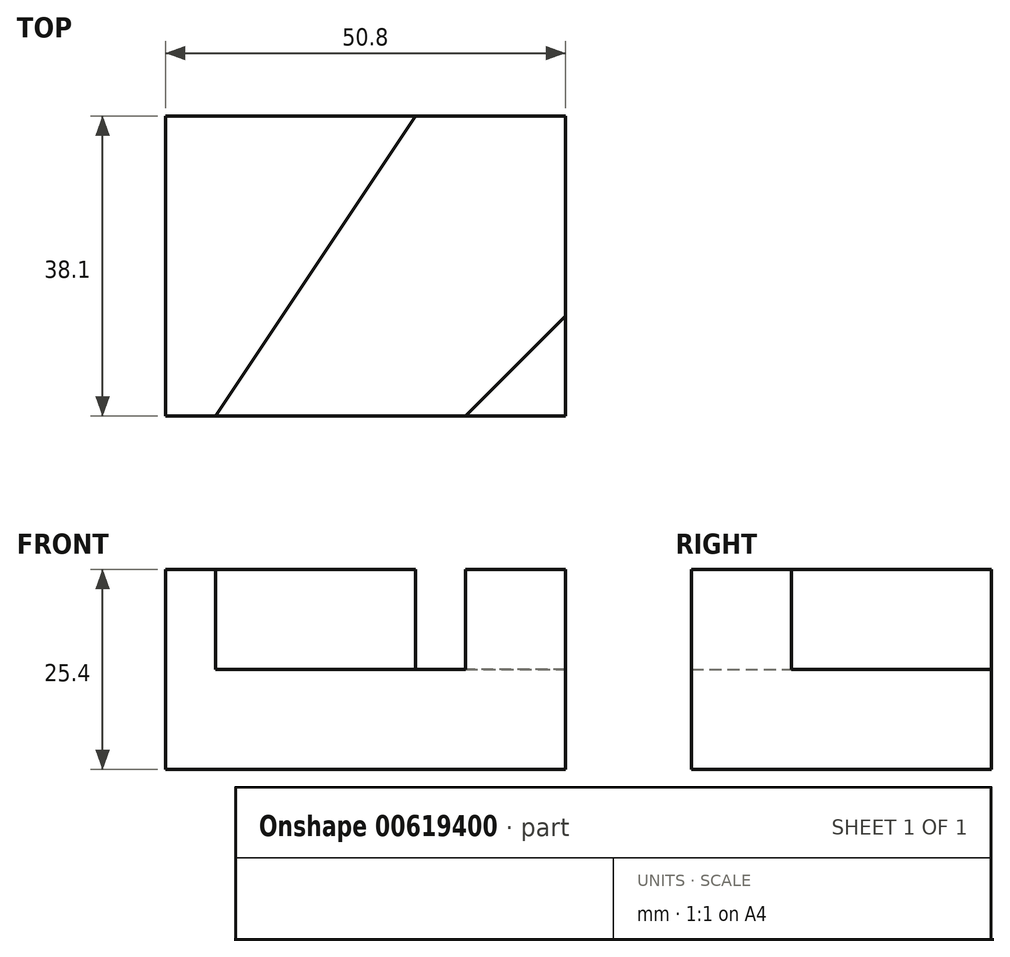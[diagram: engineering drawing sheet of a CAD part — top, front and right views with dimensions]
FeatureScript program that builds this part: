
annotation { "Feature Type Name" : "Feature", "Feature Type Description" : "" }
export const myFeature = defineFeature(function(context is Context, id is Id, definition is map)
    precondition{}
    {
        {
            var Q0;
            Q0=qCreatedBy(makeId("Right.planeOp"),FACE);
            var sketch = newSketch(context, id + "F0", { "sketchPlane" : qUnion([Q0])});
            skLineSegment(sketch, "E0", {"start": v(0, 0) * mm, "end": v(38.1, 0) * mm});
            skLineSegment(sketch, "E1", {"start": v(0, 0) * mm, "end": v(0, 12.7) * mm});
            skLineSegment(sketch, "E2", {"start": v(0, 12.7) * mm, "end": v(38.1, 12.7) * mm});
            skLineSegment(sketch, "E3", {"start": v(38.1, 12.7) * mm, "end": v(38.1, 0) * mm});
            skSolve(sketch);
        }
        {
            var Q0;
            Q0 = qSketchRegion(id + "F0", true);
            extrude(context, id + "F1", {"entities" : qUnion([Q0]), "depth" : 50.8 * mm, "offsetDistance" : 25.4 * mm});
        }
        {
            var Q0;
            Q0=makeQuery(id+"F1.opExtrude","SWEPT_FACE",FACE,{"disambiguationData":[OSD([sQuery(id+"F0.wireOp",EDGE,"E2")])]});
            var sketch = newSketch(context, id + "F2", { "sketchPlane" : qUnion([Q0])});
            skLineSegment(sketch, "E4", {"start": v(0, 38.1) * mm, "end": v(31.75, 38.1) * mm});
            skLineSegment(sketch, "E5", {"start": v(0, 38.1) * mm, "end": v(0, 0) * mm});
            skLineSegment(sketch, "E6", {"start": v(0, 0) * mm, "end": v(6.35, 0) * mm});
            skLineSegment(sketch, "E7", {"start": v(6.35, 0) * mm, "end": v(31.75, 38.1) * mm});
            skSolve(sketch);
        }
        {
            var Q0;
            Q0 = qSketchRegion(id + "F2", true);
            extrude(context, id + "F3", {"entities" : qUnion([Q0]), "operationType" : NewBodyOperationType.ADD, "depth" : 12.7 * mm, "offsetDistance" : 25.4 * mm});
        }
        {
            var Q0;
            Q0=makeQuery(id+"F1.opExtrude","SWEPT_FACE",FACE,{"disambiguationData":[OSD([sQuery(id+"F0.wireOp",EDGE,"E2")])]});
            var sketch = newSketch(context, id + "F4", { "sketchPlane" : qUnion([Q0])});
            skLineSegment(sketch, "E8", {"start": v(50.8, 0) * mm, "end": v(38.1, 0) * mm});
            skLineSegment(sketch, "E9", {"start": v(50.8, 0) * mm, "end": v(50.8, 12.7) * mm});
            skLineSegment(sketch, "E10", {"start": v(38.1, 0) * mm, "end": v(50.8, 12.7) * mm});
            skSolve(sketch);
        }
        {
            var Q0;
            Q0 = qSketchRegion(id + "F4", true);
            extrude(context, id + "F5", {"entities" : qUnion([Q0]), "operationType" : NewBodyOperationType.ADD, "depth" : 12.7 * mm, "offsetDistance" : 25.4 * mm});
        }
    });
